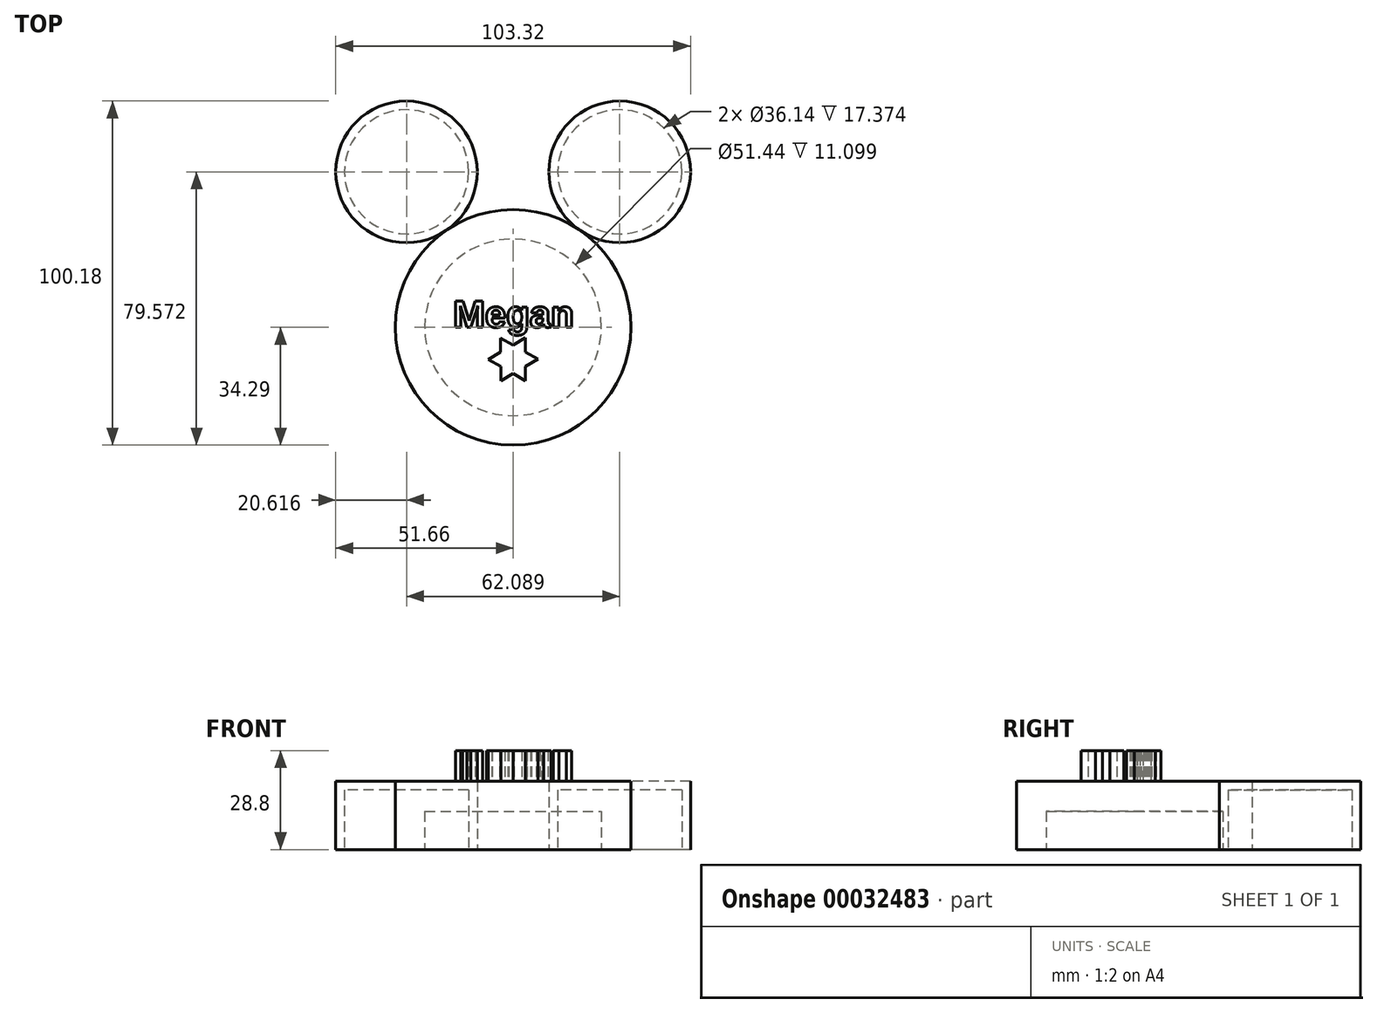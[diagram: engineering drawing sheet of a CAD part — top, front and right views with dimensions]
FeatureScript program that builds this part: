
annotation { "Feature Type Name" : "Feature", "Feature Type Description" : "" }
export const myFeature = defineFeature(function(context is Context, id is Id, definition is map)
    precondition{}
    {
        {
            var Q0;
            Q0=qCreatedBy(makeId("Top.planeOp"),FACE);
            var sketch = newSketch(context, id + "F0", { "sketchPlane" : qUnion([Q0])});
            skCircle(sketch, "E0", {"center": v(0, 0) * mm, "radius": 34.3 * mm});
            skCircle(sketch, "E1", {"center": v(31.04, 45.28) * mm, "radius": 20.61 * mm});
            skCircle(sketch, "E2", {"center": v(-31.04, 45.28) * mm, "radius": 20.61 * mm});
            skSolve(sketch);
        }
        {
            var Q0;
            Q0=makeQuery(id+"F0.imprint","IMPRINT",FACE,{"disambiguationData":[TD([[makeQuery(id+"F0.imprint","IMPRINT",EDGE,{"derivedFrom":sQuery(id+"F0.wireOp",EDGE,"E0")}),1.0]])]});
            var Q1;
            Q1=makeQuery(id+"F0.imprint","IMPRINT",FACE,{"disambiguationData":[TD([[makeQuery(id+"F0.imprint","IMPRINT",EDGE,{"derivedFrom":sQuery(id+"F0.wireOp",EDGE,"E1")}),1.0]])]});
            var Q2;
            Q2=makeQuery(id+"F0.imprint","IMPRINT",FACE,{"disambiguationData":[TD([[makeQuery(id+"F0.imprint","IMPRINT",EDGE,{"derivedFrom":sQuery(id+"F0.wireOp",EDGE,"E2")}),1.0]])]});
            extrude(context, id + "F1", {"entities" : qUnion([Q0, Q1, Q2]), "depth" : 19.91 * mm});
        }
        {
            var Q0;
            Q0=makeQuery(id+"F1.opExtrude","CAP_FACE",FACE,{"disambiguationData":[OSD([sQuery(id+"F0.wireOp",EDGE,"E0")])],"isStart":false});
            var sketch = newSketch(context, id + "F2", { "sketchPlane" : qUnion([Q0])});
            skText(sketch, "E3", { "text": "Megan", "fontName": "Arimo-Bold.ttf"});
            skCircle(sketch, "E4.cCircle", {"center": v(0, -9.33) * mm, "radius": 3.61 * mm, "construction": true});
            skLineSegment(sketch, "E4.0", {"start": v(3.61, -3.07) * mm, "end": v(3.61, -15.58) * mm});
            skLineSegment(sketch, "E4.1", {"start": v(3.61, -15.58) * mm, "end": v(-7.22, -9.33) * mm});
            skLineSegment(sketch, "E4.2", {"start": v(-7.22, -9.33) * mm, "end": v(3.61, -3.07) * mm});
            skPoint(sketch, "E4.0.midPoint", {"position": v(3.61, -9.33) * mm});
            skLineSegment(sketch, "E5.0", {"start": v(-3.65, -3.1) * mm, "end": v(7.22, -9.28) * mm});
            skLineSegment(sketch, "E5.1", {"start": v(7.22, -9.28) * mm, "end": v(-3.57, -15.6) * mm});
            skLineSegment(sketch, "E5.2", {"start": v(-3.57, -15.6) * mm, "end": v(-3.65, -3.1) * mm});
            skPoint(sketch, "E5.0.midPoint", {"position": v(1.79, -6.2) * mm});
            const initialGuessF2  = {"E3": [-0.01746, 0, 1, 0, 0.00801]};
            skSetInitialGuess(sketch, initialGuessF2);
            skSolve(sketch);
        }
        {
            var Q0;
            Q0=makeQuery(id+"F2.imprint","IMPRINT",FACE,{"disambiguationData":[TD([[makeQuery(id+"F2.imprint","IMPRINT",EDGE,{"derivedFrom":sQuery(id+"F2.wireOp",EDGE,"E3.sketch_text.stroke-0")}),-1.0]])]});
            var Q1;
            Q1=makeQuery(id+"F2.imprint","IMPRINT",FACE,{"disambiguationData":[TD([[makeQuery(id+"F2.imprint","IMPRINT",EDGE,{"derivedFrom":sQuery(id+"F2.wireOp",EDGE,"E3.sketch_text.stroke-107")}),-1.0]])]});
            var Q2;
            Q2=makeQuery(id+"F2.imprint","IMPRINT",FACE,{"disambiguationData":[TD([[makeQuery(id+"F2.imprint","IMPRINT",EDGE,{"derivedFrom":sQuery(id+"F2.wireOp",EDGE,"E3.sketch_text.stroke-21")}),-1.0]])]});
            var Q3;
            Q3=makeQuery(id+"F2.imprint","IMPRINT",FACE,{"disambiguationData":[TD([[makeQuery(id+"F2.imprint","IMPRINT",EDGE,{"derivedFrom":sQuery(id+"F2.wireOp",EDGE,"E3.sketch_text.stroke-39")}),-1.0]])]});
            var Q4;
            Q4=makeQuery(id+"F2.imprint","IMPRINT",FACE,{"disambiguationData":[TD([[makeQuery(id+"F2.imprint","IMPRINT",EDGE,{"derivedFrom":sQuery(id+"F2.wireOp",EDGE,"E3.sketch_text.stroke-69")}),-1.0]])]});
            var Q5;
            {var subQ1=sQuery(id+"F2.wireOp",EDGE,"E4.2");var subQ3=sQuery(id+"F2.wireOp",EDGE,"E4.0");var subQ5=makeQuery(id+"F2.imprint","INTERSECT",VERTEX,{"derivedFrom":[subQ3,subQ1]});Q5=makeQuery(id+"F2.imprint","IMPRINT",FACE,{"disambiguationData":[TD([[makeQuery(id+"F2.imprint","IMPRINT",EDGE,{"disambiguationData":[TD([[subQ5,-1.0]])],"derivedFrom":subQ3}),-1.0]])]});}
            var Q6;
            {var subQ1=sQuery(id+"F2.wireOp",EDGE,"E4.0");var subQ3=sQuery(id+"F2.wireOp",EDGE,"E5.0");var subQ5=makeQuery(id+"F2.imprint","INTERSECT",VERTEX,{"derivedFrom":[subQ1,subQ3]});Q6=makeQuery(id+"F2.imprint","IMPRINT",FACE,{"disambiguationData":[TD([[makeQuery(id+"F2.imprint","IMPRINT",EDGE,{"disambiguationData":[TD([[subQ5,-1.0]])],"derivedFrom":subQ1}),1.0]])]});}
            var Q7;
            {var subQ1=sQuery(id+"F2.wireOp",EDGE,"E4.1");var subQ3=sQuery(id+"F2.wireOp",EDGE,"E4.0");var subQ5=makeQuery(id+"F2.imprint","INTERSECT",VERTEX,{"derivedFrom":[subQ3,subQ1]});Q7=makeQuery(id+"F2.imprint","IMPRINT",FACE,{"disambiguationData":[TD([[makeQuery(id+"F2.imprint","IMPRINT",EDGE,{"disambiguationData":[TD([[subQ5,1.0]])],"derivedFrom":subQ3}),-1.0]])]});}
            var Q8;
            {var subQ1=sQuery(id+"F2.wireOp",EDGE,"E4.1");var subQ3=sQuery(id+"F2.wireOp",EDGE,"E5.1");var subQ5=makeQuery(id+"F2.imprint","INTERSECT",VERTEX,{"derivedFrom":[subQ1,subQ3]});Q8=makeQuery(id+"F2.imprint","IMPRINT",FACE,{"disambiguationData":[TD([[makeQuery(id+"F2.imprint","IMPRINT",EDGE,{"disambiguationData":[TD([[subQ5,-1.0]])],"derivedFrom":subQ1}),1.0]])]});}
            var Q9;
            {var subQ1=sQuery(id+"F2.wireOp",EDGE,"E4.2");var subQ3=sQuery(id+"F2.wireOp",EDGE,"E4.1");var subQ5=makeQuery(id+"F2.imprint","INTERSECT",VERTEX,{"derivedFrom":[subQ3,subQ1]});Q9=makeQuery(id+"F2.imprint","IMPRINT",FACE,{"disambiguationData":[TD([[makeQuery(id+"F2.imprint","IMPRINT",EDGE,{"disambiguationData":[TD([[subQ5,1.0]])],"derivedFrom":subQ3}),-1.0]])]});}
            var Q10;
            {var subQ0=sQuery(id+"F2.wireOp",EDGE,"E5.2");var subQ1=sQuery(id+"F2.wireOp",EDGE,"E4.2");var subQ2=makeQuery(id+"F2.imprint","INTERSECT",VERTEX,{"derivedFrom":[subQ1,subQ0]});Q10=makeQuery(id+"F2.imprint","IMPRINT",FACE,{"disambiguationData":[TD([[makeQuery(id+"F2.imprint","IMPRINT",EDGE,{"disambiguationData":[TD([[subQ2,-1.0]])],"derivedFrom":subQ1}),1.0]])]});}
            var Q11;
            {var subQ3=sQuery(id+"F2.wireOp",EDGE,"E4.0");var subQ5=sQuery(id+"F2.wireOp",EDGE,"E5.0");var subQ8=makeQuery(id+"F2.imprint","INTERSECT",VERTEX,{"derivedFrom":[subQ3,subQ5]});Q11=makeQuery(id+"F2.imprint","IMPRINT",FACE,{"disambiguationData":[TD([[makeQuery(id+"F2.imprint","IMPRINT",EDGE,{"disambiguationData":[TD([[subQ8,-1.0]])],"derivedFrom":subQ3}),-1.0]])]});}
            extrude(context, id + "F3", {"entities" : qUnion([Q0, Q1, Q2, Q3, Q4, Q5, Q6, Q7, Q8, Q9, Q10, Q11]), "operationType" : NewBodyOperationType.ADD, "depth" : 8.9 * mm});
        }
        {
            var Q0;
            Q0=makeQuery(id+"F1.opExtrude","CAP_FACE",FACE,{"disambiguationData":[OSD([sQuery(id+"F0.wireOp",EDGE,"E0")])],"isStart":true});
            var sketch = newSketch(context, id + "F4", { "sketchPlane" : qUnion([Q0])});
            skCircle(sketch, "E6", {"center": v(0, 0) * mm, "radius": 25.72 * mm});
            skSolve(sketch);
        }
        {
            var Q0;
            Q0=makeQuery(id+"F4.imprint","IMPRINT",FACE,{"disambiguationData":[TD([[makeQuery(id+"F4.imprint","IMPRINT",EDGE,{"derivedFrom":sQuery(id+"F4.wireOp",EDGE,"E6")}),1.0]])]});
            extrude(context, id + "F5", {"entities" : qUnion([Q0]), "operationType" : NewBodyOperationType.REMOVE, "oppositeDirection" : true, "depth" : 11.1 * mm});
        }
        {
            var Q0;
            Q0=makeQuery(id+"F1.opExtrude","CAP_FACE",FACE,{"disambiguationData":[OSD([sQuery(id+"F0.wireOp",EDGE,"E1")])],"isStart":true});
            var Q1;
            Q1=makeQuery(id+"F1.opExtrude","CAP_FACE",FACE,{"disambiguationData":[OSD([sQuery(id+"F0.wireOp",EDGE,"E2")])],"isStart":true});
            shell(context, id + "F6", {"entities" : qUnion([Q0, Q1]), "thickness" : 2.54 * mm});
        }
    });
